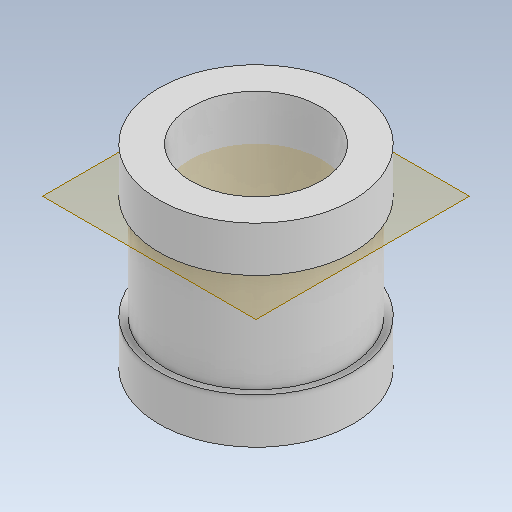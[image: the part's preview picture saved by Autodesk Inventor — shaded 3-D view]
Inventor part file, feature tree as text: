
AUTODESK INVENTOR PART (.ipt)
format: ipt  version: 2023 (Build 270158000, 158)  size: 128,000 bytes
history: native  units: mm
features: extrude x2, sketch x2, plane x1, projected_geometry x1
ambient origin geometry x8: Origin, YZ Plane, XZ Plane, XY Plane, X Axis, Y Axis, Z Axis, Center Point
bodies: Solid1 (feature_tree)
feature tree (6):
  extrude  "Extrusion1"  Depth=3.0mm
  plane  "Work Plane1"
  extrude  "Extrusion2"  [1 undecoded]
  sketch  "Sketch1"  dims[d0=3.0mm d1=2.0mm]
  sketch  "Sketch2"  dims[d2=3.0mm d3=0.0mm d4=-0.7mm d5=2.8mm d6=1.6mm d7=0.0mm]
  projected_geometry  "Projected Loop1"
note: 1 required parameter value undecoded (feature->parameter linkage not recoverable at this tier; creation-order binding heuristic only, values carry confidence <= 0.55)
